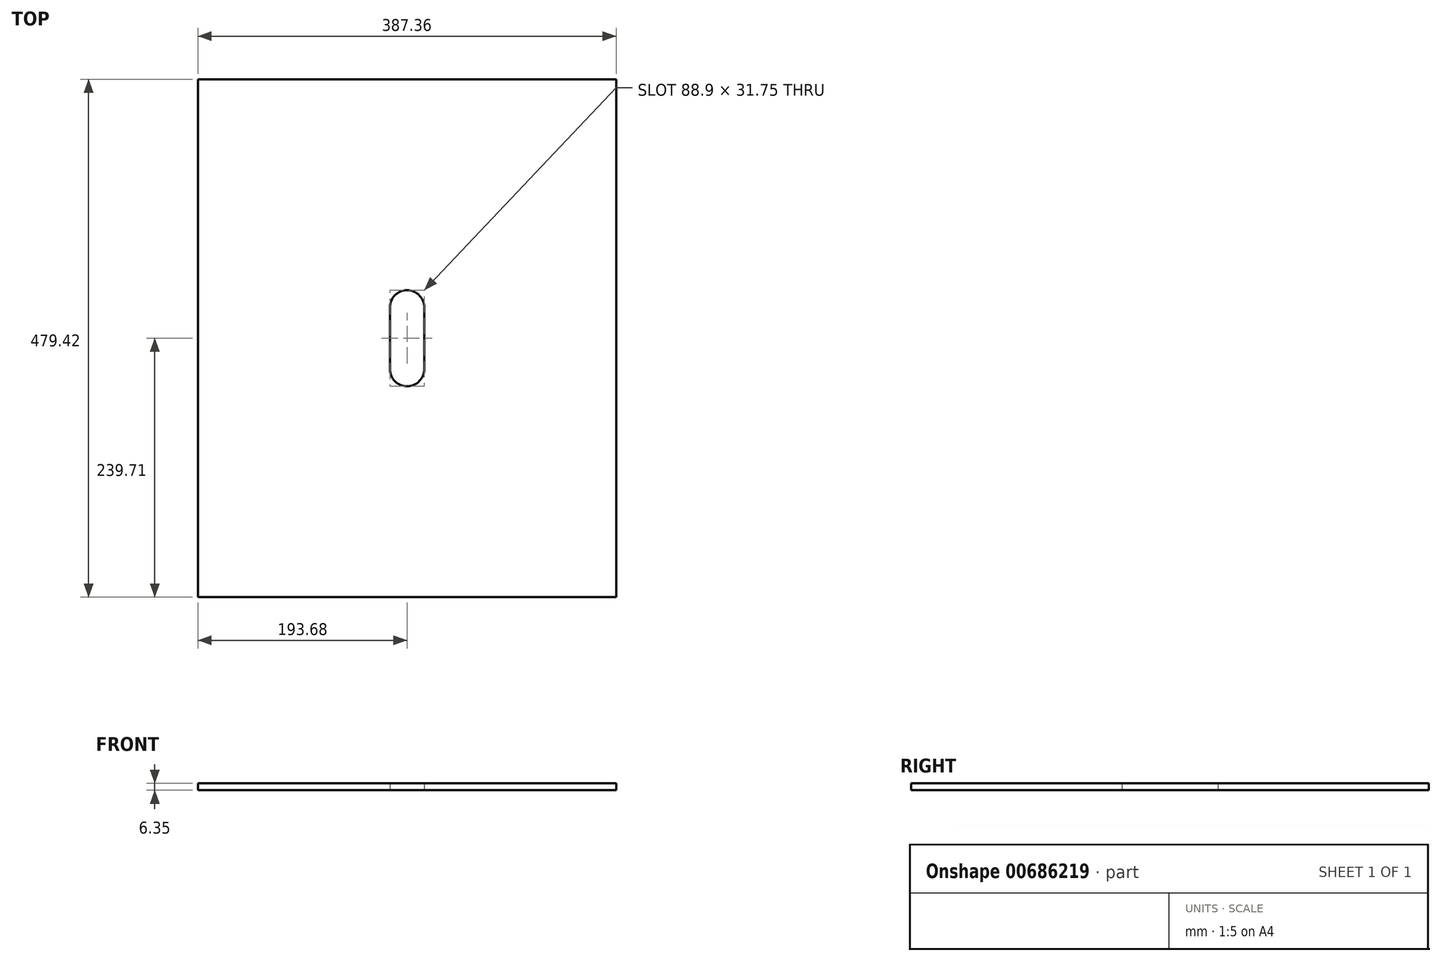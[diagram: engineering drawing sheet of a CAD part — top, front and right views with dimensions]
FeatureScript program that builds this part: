
annotation { "Feature Type Name" : "Feature", "Feature Type Description" : "" }
export const myFeature = defineFeature(function(context is Context, id is Id, definition is map)
    precondition{}
    {
        {
            var Q0;
            Q0=qCreatedBy(makeId("Top.planeOp"),FACE);
            var sketch = newSketch(context, id + "F0", { "sketchPlane" : qUnion([Q0])});
            skLineSegment(sketch, "E0.bottom", {"start": v(-193.67, 239.71) * mm, "end": v(193.68, 239.71) * mm});
            skLineSegment(sketch, "E0.top", {"start": v(-193.68, -239.71) * mm, "end": v(193.67, -239.71) * mm});
            skLineSegment(sketch, "E0.left", {"start": v(-193.67, 239.71) * mm, "end": v(-193.68, -239.71) * mm});
            skLineSegment(sketch, "E0.right", {"start": v(193.68, 239.71) * mm, "end": v(193.67, -239.71) * mm});
            skPoint(sketch, "E0.middle", {"position": v(0, 0) * mm});
            skLineSegment(sketch, "E1.left", {"start": v(-15.88, 28.57) * mm, "end": v(-15.88, -28.57) * mm});
            skLineSegment(sketch, "E1.right", {"start": v(15.87, 28.57) * mm, "end": v(15.87, -28.57) * mm});
            skArc(sketch, "E2", {"start": v(15.87, 28.57) * mm, "mid": v(0, 44.45) * mm, "end": v(-15.87, 28.57) * mm});
            skArc(sketch, "E3", {"start": v(-15.87, -28.57) * mm, "mid": v(0, -44.45) * mm, "end": v(15.87, -28.57) * mm});
            skPoint(sketch, "E4.orphan", {"position": v(-15.88, 67.91) * mm});
            skPoint(sketch, "E5.orphan", {"position": v(15.87, 115.4) * mm});
            skPoint(sketch, "E6.orphan", {"position": v(15.88, -67.91) * mm});
            skPoint(sketch, "E7.orphan", {"position": v(-15.88, -115.4) * mm});
            skPoint(sketch, "E8", {"position": v(0, 44.45) * mm});
            skPoint(sketch, "E9", {"position": v(0, -44.45) * mm});
            skLineSegment(sketch, "E10", {"start": v(0, 44.45) * mm, "end": v(0, -44.45) * mm, "construction": true});
            skSolve(sketch);
        }
        {
            var Q0;
            Q0 = qSketchRegion(id + "F0", true);
            extrude(context, id + "F1", {"entities" : qUnion([Q0]), "depth" : 6.35 * mm, "offsetDistance" : 25.4 * mm});
        }
    });
